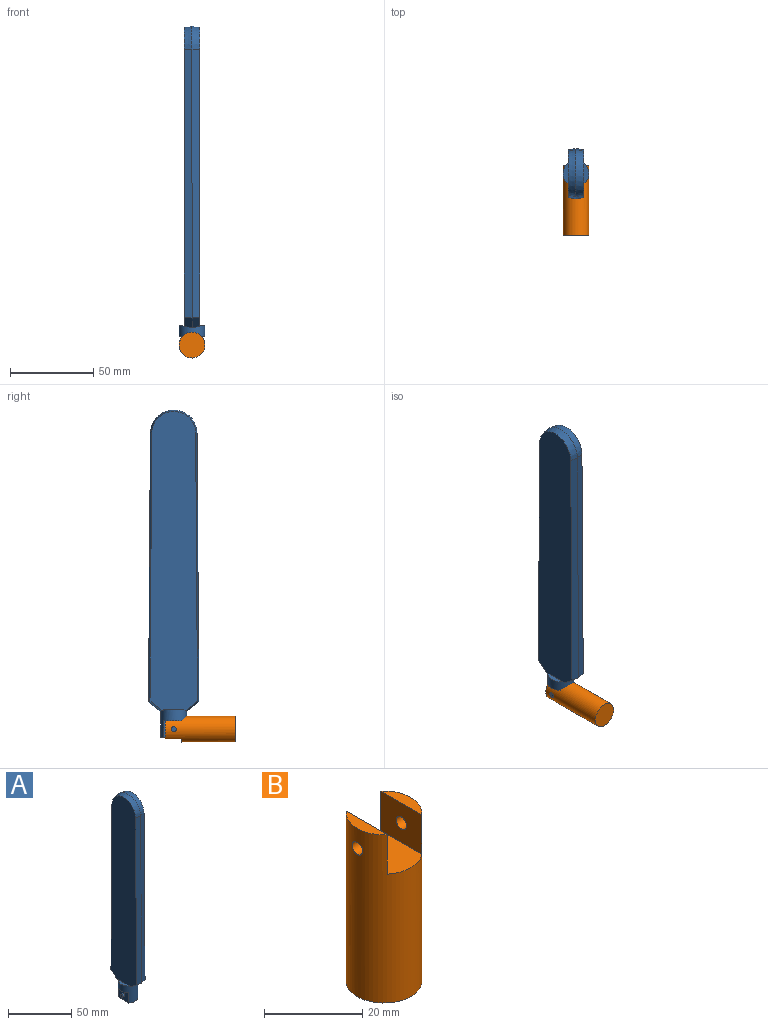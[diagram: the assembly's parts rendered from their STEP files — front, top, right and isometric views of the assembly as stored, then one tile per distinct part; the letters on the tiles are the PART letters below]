
ASSEMBLY  parts=2 mates=1
PART A: 28 faces, bbox 15.5x30.2x196.3 mm
  f0: plane 3.8x1.57mm, normal (0.17,0,-0.98), area 1.8mm2, adj f2,f4,f18
  f1: plane 3.8x1.57mm, normal (-0.17,0,-0.98), area 1.8mm2, adj f11,f15,f18
  f2: plane 179.17x28.48mm, normal (1,0,0), area 4788.3mm2, adj f0,f3,f4,f5,f6,f7,f8,f18
  f3: plane 160.98x4.75mm, normal (0.17,0.98,0.01), area 775.5mm2, adj f2,f4,f8,f14
  f4: plane 7.63x6.26mm, normal (0.17,0.61,-0.77), area 43.6mm2, adj f0,f2,f3,f13,f18
  f5: plane 3.8x1.57mm, normal (0.17,0,-0.98), area 1.8mm2, adj f2,f6,f18
  f6: plane 7.63x6.26mm, normal (0.17,-0.61,-0.77), area 43.6mm2, adj f2,f5,f7,f11,f18
  f7: plane 160.98x4.75mm, normal (0.17,-0.98,0.01), area 775.5mm2, adj f2,f6,f8,f10
  f8: cone r=14mm half-angle=10deg, axis (-1,0,0), area 205.8mm2, adj f2,f3,f7,f9
  f9: cone r=14mm half-angle=10deg, axis (1,0,0), area 205.8mm2, adj f8,f10,f14,f15
  f10: plane 160.98x4.75mm, normal (-0.17,-0.98,0.01), area 775.5mm2, adj f7,f9,f11,f15
  f11: plane 7.63x6.26mm, normal (-0.17,-0.61,-0.77), area 43.6mm2, adj f1,f6,f10,f15,f18
  f12: plane 3.8x1.57mm, normal (-0.17,0,-0.98), area 1.8mm2, adj f13,f15,f18
  f13: plane 7.63x6.26mm, normal (-0.17,0.61,-0.77), area 43.6mm2, adj f4,f12,f14,f15,f18
  f14: plane 160.98x4.75mm, normal (-0.17,0.98,0.01), area 775.5mm2, adj f3,f9,f13,f15
  f15: plane 179.17x28.48mm, normal (-1,0,0), area 4788.3mm2, adj f1,f9,f10,f11,f12,f13,f14,f16
  f16: plane 12.25x3mm, normal (0,0,1), area 25.6mm2, adj f15,f18
  f17: plane 15.5x10mm, normal (0,0,-1), area 143.4mm2, adj f18,f19,f21
  f18: cylinder r=7.75mm len=16.5mm, axis (0,0,1), area 522.4mm2, adj f0,f1,f2,f4,f5,f6,f11,f12
  f19: plane 11.84x10mm, normal (1,0,0), area 111.4mm2, adj f17,f18,f20,f23
  f20: plane 11.84x2.75mm, normal (0,0,-1), area 22.6mm2, adj f18,f19
  f21: plane 11.84x10mm, normal (-1,0,0), area 111.4mm2, adj f17,f18,f22,f25
  f22: plane 11.84x2.75mm, normal (0,0,-1), area 22.6mm2, adj f18,f21
  f23: cylinder r=1.5mm len=3mm, axis (-1,0,0), area 18.8mm2, adj f19,f24
  f24: plane 3x3mm, normal (1,0,0), area 7.1mm2, adj f23
  f25: cylinder r=1.5mm len=3mm, axis (1,0,0), area 18.8mm2, adj f21,f26
  f26: plane 3x3mm, normal (-1,0,0), area 7.1mm2, adj f25
  f27: plane 12.25x3mm, normal (0,0,1), area 25.6mm2, adj f2,f18
PART B: 9 faces, bbox 15.5x15.5x42 mm
  f0: cylinder r=7.75mm len=42mm, axis (0,0,-1), area 1817.4mm2, adj f1,f2,f3,f4,f5,f6,f7,f8
  f1: plane 11.84x2.75mm, normal (0,0,1), area 22.6mm2, adj f0,f6
  f2: plane 11.84x2.75mm, normal (0,0,1), area 22.6mm2, adj f0,f5
  f3: plane 15.5x15.5mm, normal (0,0,-1), area 188.7mm2, adj f0
  f4: plane 15.5x10mm, normal (0,0,1), area 143.4mm2, adj f0,f5,f6
  f5: plane 11.84x9.82mm, normal (-1,0,0), area 109.2mm2, adj f0,f2,f4,f7
  f6: plane 11.84x9.82mm, normal (1,0,0), area 109.2mm2, adj f0,f1,f4,f8
  f7: cylinder r=1.5mm len=3mm, axis (-1,0,0), area 25.2mm2, adj f0,f5
  f8: cylinder r=1.5mm len=3mm, axis (1,0,0), area 25.2mm2, adj f0,f6
PLACE A rot(axis=(-1,0,0),0deg) t=(28.55,49.59,34.02)mm
PLACE B rot(axis=(-1,0,0),90deg) t=(28.55,-2.63,39.02)mm
MATE planar A.f25 <-> B.f7  axis (1,0,0) through (33.55,34.37,39.02)mm
